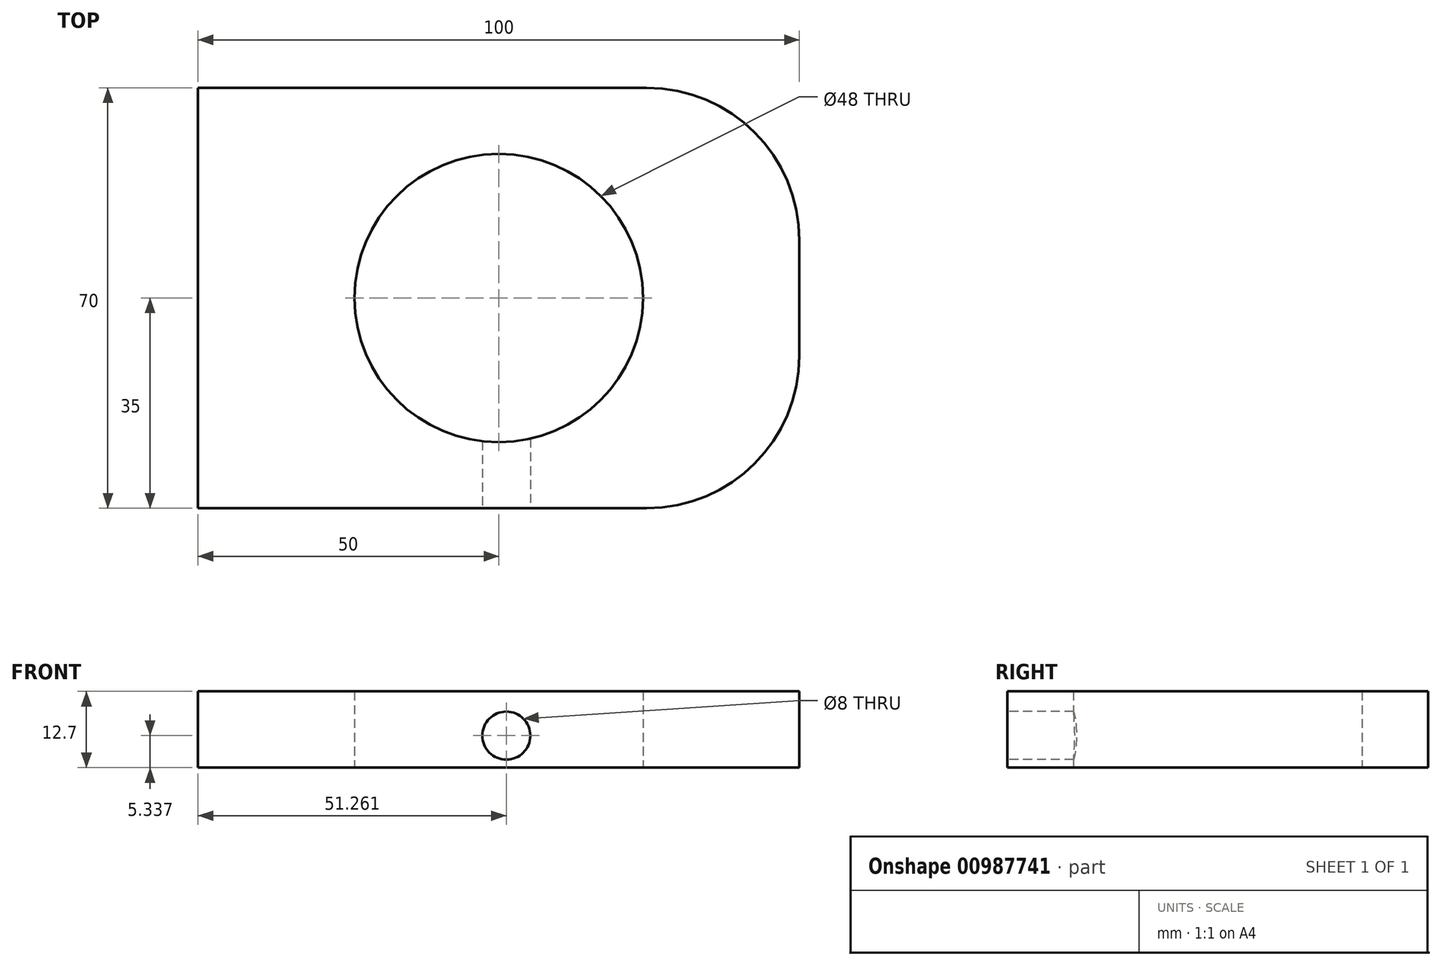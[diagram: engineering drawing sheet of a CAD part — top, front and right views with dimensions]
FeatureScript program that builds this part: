
annotation { "Feature Type Name" : "Feature", "Feature Type Description" : "" }
export const myFeature = defineFeature(function(context is Context, id is Id, definition is map)
    precondition{}
    {
        {
            var Q0;
            Q0=qCreatedBy(makeId("Top.planeOp"),FACE);
            var sketch = newSketch(context, id + "F0", { "sketchPlane" : qUnion([Q0])});
            skLineSegment(sketch, "E0.bottom", {"start": v(-50, 35) * mm, "end": v(50, 35) * mm});
            skLineSegment(sketch, "E0.top", {"start": v(-50, -35) * mm, "end": v(50, -35) * mm});
            skLineSegment(sketch, "E0.left", {"start": v(-50, 35) * mm, "end": v(-50, -35) * mm});
            skLineSegment(sketch, "E0.right", {"start": v(50, 35) * mm, "end": v(50, -35) * mm});
            skPoint(sketch, "E0.middle", {"position": v(0, 0) * mm});
            skCircle(sketch, "E1", {"center": v(0, 0) * mm, "radius": 24 * mm});
            skSolve(sketch);
        }
        {
            var Q0;
            Q0=makeQuery(id+"F0.imprint","IMPRINT",FACE,{"disambiguationData":[TD([[makeQuery(id+"F0.imprint","IMPRINT",EDGE,{"derivedFrom":sQuery(id+"F0.wireOp",EDGE,"E0.bottom")}),-1.0]])]});
            extrude(context, id + "F1", {"entities" : qUnion([Q0]), "depth" : 12.7 * mm, "offsetDistance" : 25.4 * mm});
        }
        {
            var Q0;
            Q0=makeQuery(id+"F1.opExtrude","SWEPT_EDGE",EDGE,{"disambiguationData":[OSD([sQuery(id+"F0.wireOp",EDGE,"E0.top"),sQuery(id+"F0.wireOp",EDGE,"E0.right")])]});
            var Q1;
            Q1=makeQuery(id+"F1.opExtrude","SWEPT_EDGE",EDGE,{"disambiguationData":[OSD([sQuery(id+"F0.wireOp",EDGE,"E0.bottom"),sQuery(id+"F0.wireOp",EDGE,"E0.right")])]});
            fillet(context, id + "F2", {"entities" : qUnion([Q0, Q1]), "radius" : 25.4 * mm, "tangentPropagation" : true, "allowEdgeOverflow" : false});
        }
        {
            var Q0;
            Q0=makeQuery(id+"F1.opExtrude","SWEPT_FACE",FACE,{"disambiguationData":[OSD([sQuery(id+"F0.wireOp",EDGE,"E0.top")])]});
            var sketch = newSketch(context, id + "F3", { "sketchPlane" : qUnion([Q0])});
            skCircle(sketch, "E2", {"center": v(1.26, 5.34) * mm, "radius": 4 * mm});
            skSolve(sketch);
        }
        {
            var Q0;
            Q0=sQuery(id+"F3.wireOp",VERTEX,"E2.center");
            var Q1;
            Q1=makeQuery(id+"F1.opExtrude","SWEPT_BODY",BODY,{"disambiguationData":[OSD([sQuery(id+"F0.wireOp",EDGE,"E0.bottom"),sQuery(id+"F0.wireOp",EDGE,"E0.top"),sQuery(id+"F0.wireOp",EDGE,"E0.left"),sQuery(id+"F0.wireOp",EDGE,"E0.right"),sQuery(id+"F0.wireOp",EDGE,"E1")])]});
            hole(context, id + "F4", {"style" : HoleStyle.SIMPLE, "endStyle" : HoleEndStyle.BLIND, "holeDiameter" : 8 * mm, "majorDiameter" : 6.35 * mm, "holeDepth" : 12.7 * mm, "isTappedThrough" : true, "tappedDepth" : 12.7 * mm, "tapClearance" : 3, "locations" : qUnion([Q0]), "scope" : qUnion([Q1])});
        }
    });
